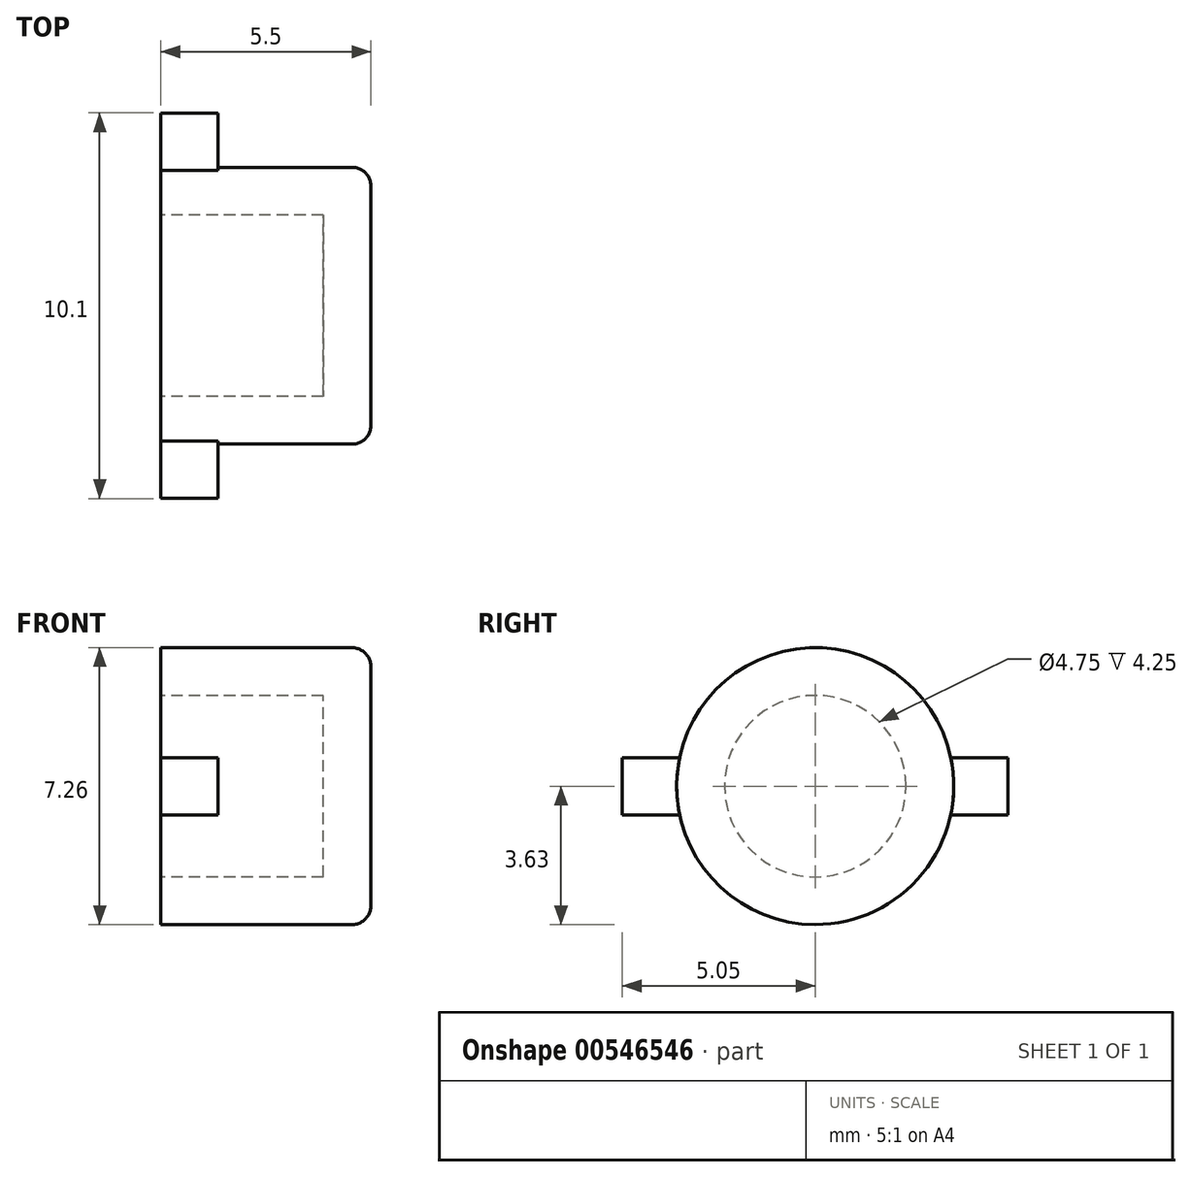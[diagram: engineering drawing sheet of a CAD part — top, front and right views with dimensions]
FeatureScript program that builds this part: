
annotation { "Feature Type Name" : "Feature", "Feature Type Description" : "" }
export const myFeature = defineFeature(function(context is Context, id is Id, definition is map)
    precondition{}
    {
        {
            var Q0;
            Q0=qCreatedBy(makeId("Right.planeOp"),FACE);
            var sketch = newSketch(context, id + "F0", { "sketchPlane" : qUnion([Q0])});
            skCircle(sketch, "E0", {"center": v(0, 0) * mm, "radius": 3.62 * mm});
            skSolve(sketch);
        }
        {
            var Q0;
            Q0=makeQuery(id+"F0.imprint","IMPRINT",FACE,{"disambiguationData":[TD([[makeQuery(id+"F0.imprint","IMPRINT",EDGE,{"derivedFrom":sQuery(id+"F0.wireOp",EDGE,"E0")}),1.0]])]});
            extrude(context, id + "F1", {"entities" : qUnion([Q0]), "endBound" : BoundingType.SYMMETRIC, "depth" : 5.5 * mm, "offsetDistance" : 25 * mm});
        }
        {
            var Q0;
            Q0=makeQuery(id+"F1.opExtrude","CAP_FACE",FACE,{"disambiguationData":[OSD([sQuery(id+"F0.wireOp",EDGE,"E0")])],"isStart":false});
            fillet(context, id + "F2", {"entities" : qUnion([Q0]), "radius" : 0.5 * mm, "tangentPropagation" : true, "allowEdgeOverflow" : false});
        }
        {
            var Q0;
            Q0=makeQuery(id+"F1.opExtrude","CAP_FACE",FACE,{"disambiguationData":[OSD([sQuery(id+"F0.wireOp",EDGE,"E0")])],"isStart":true});
            shell(context, id + "F3", {"entities" : qUnion([Q0]), "thickness" : 1.25 * mm});
        }
        {
            var Q0;
            Q0=makeQuery(id+"F1.opExtrude","CAP_FACE",FACE,{"disambiguationData":[OSD([sQuery(id+"F0.wireOp",EDGE,"E0")])],"isStart":true});
            var sketch = newSketch(context, id + "F4", { "sketchPlane" : qUnion([Q0])});
            skLineSegment(sketch, "E1.left", {"start": v(5.05, -0.75) * mm, "end": v(5.05, 0.75) * mm});
            skLineSegment(sketch, "E2.left", {"start": v(-5.05, 0.75) * mm, "end": v(-5.05, -0.75) * mm});
            skLineSegment(sketch, "E3", {"start": v(5.05, 0.75) * mm, "end": v(3.55, 0.75) * mm});
            skLineSegment(sketch, "E4", {"start": v(5.05, -0.75) * mm, "end": v(3.55, -0.75) * mm});
            skArc(sketch, "E5", {"start": v(-3.55, 0.75) * mm, "mid": v(-3.63, 0) * mm, "end": v(-3.55, -0.75) * mm});
            skLineSegment(sketch, "E6", {"start": v(-5.05, 0.75) * mm, "end": v(-3.55, 0.75) * mm});
            skLineSegment(sketch, "E7", {"start": v(-5.05, -0.75) * mm, "end": v(-3.55, -0.75) * mm});
            skArc(sketch, "E8.trimOffspring", {"start": v(3.55, -0.75) * mm, "mid": v(3.63, 0) * mm, "end": v(3.55, 0.75) * mm});
            skPoint(sketch, "E9", {"position": v(5.05, 0) * mm});
            skPoint(sketch, "E10", {"position": v(-5.05, 0) * mm});
            skSolve(sketch);
        }
        {
            var Q0;
            Q0=qSketchRegion(id+"F4",true);
            extrude(context, id + "F5", {"entities" : qUnion([Q0]), "operationType" : NewBodyOperationType.ADD, "oppositeDirection" : true, "depth" : 1.5 * mm, "offsetDistance" : 25 * mm});
        }
    });
